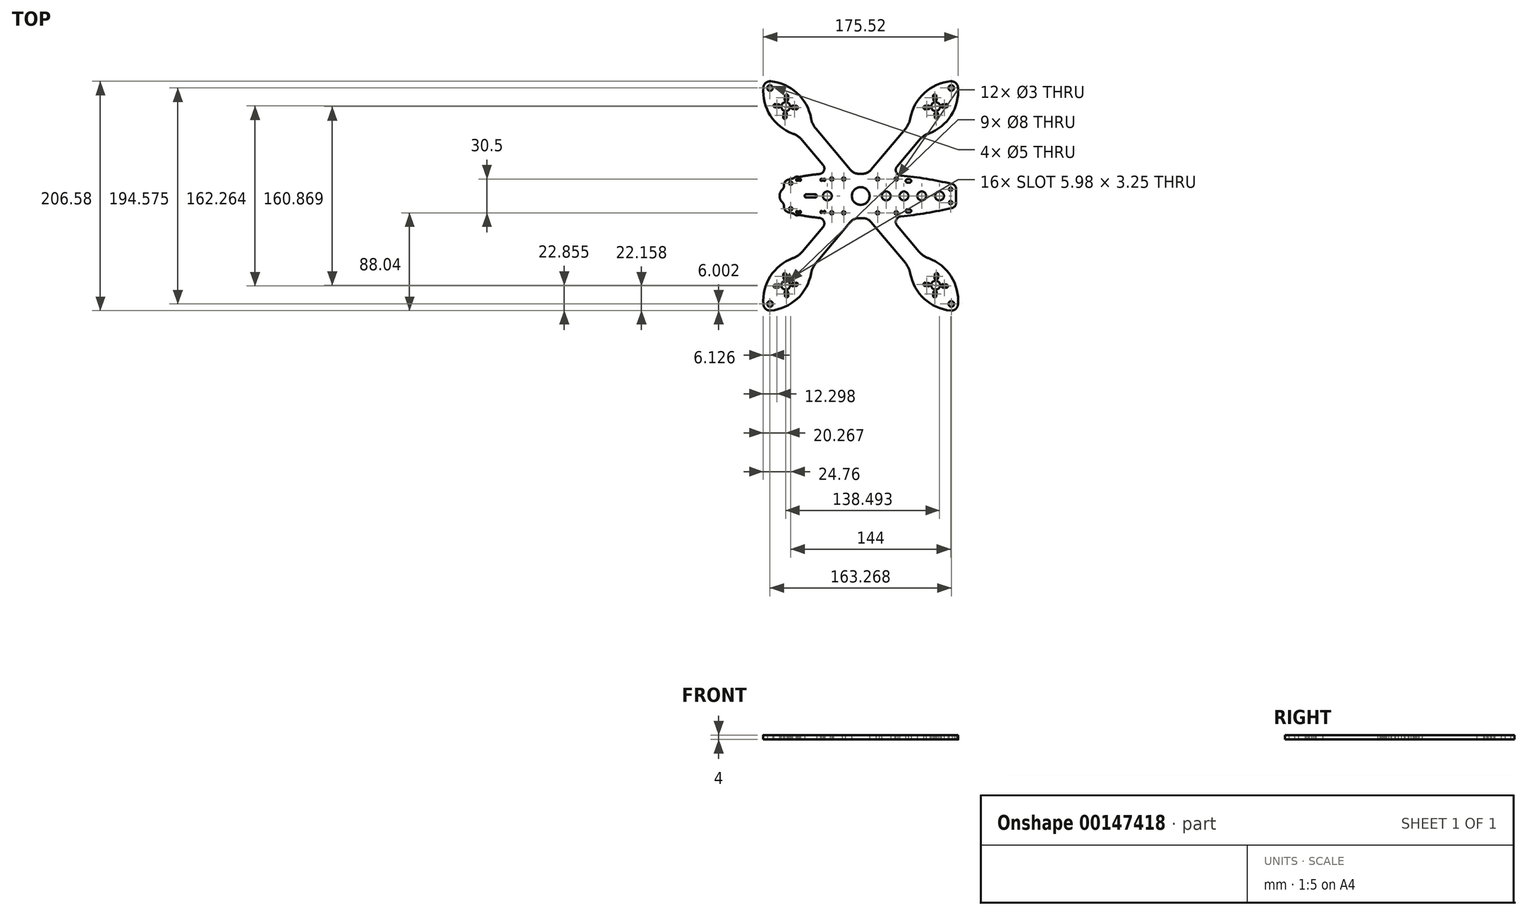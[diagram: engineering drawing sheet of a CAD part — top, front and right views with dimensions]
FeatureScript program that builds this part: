
annotation { "Feature Type Name" : "Feature", "Feature Type Description" : "" }
export const myFeature = defineFeature(function(context is Context, id is Id, definition is map)
    precondition{}
    {
        {
            var Q0;
            Q0=qCreatedBy(makeId("Top.planeOp"),FACE);
            var sketch = newSketch(context, id + "F0", { "sketchPlane" : qUnion([Q0])});
            skLineSegment(sketch, "E0.bottom", {"start": v(-1.68, 20) * mm, "end": v(1.68, 20) * mm});
            skLineSegment(sketch, "E0.left", {"start": v(-69, 9.77) * mm, "end": v(-69, 0) * mm});
            skLineSegment(sketch, "E0.right", {"start": v(86, 6.03) * mm, "end": v(86, 0) * mm});
            skArc(sketch, "E1", {"start": v(-15.25, 20) * mm, "mid": v(-16.05, 20.05) * mm, "end": v(-16.86, 20.09) * mm});
            skPoint(sketch, "E2.newPointA", {"position": v(-69, 13.5) * mm});
            skArc(sketch, "E2.filletArc", {"start": v(-65.37, 14.58) * mm, "mid": v(-67.99, 12.79) * mm, "end": v(-69, 9.77) * mm});
            skArc(sketch, "E3", {"start": v(82.11, 10.9) * mm, "mid": v(59.23, 15.39) * mm, "end": v(36.13, 18.46) * mm});
            skPoint(sketch, "E4.newPointA", {"position": v(86, 10) * mm});
            skArc(sketch, "E4.filletArc", {"start": v(86, 6.03) * mm, "mid": v(84.9, 9.15) * mm, "end": v(82.11, 10.9) * mm});
            skCircle(sketch, "E5", {"center": v(0, 0) * mm, "radius": 105 * mm, "construction": true});
            skLineSegment(sketch, "E6", {"start": v(0, 0) * mm, "end": v(67.5, 80.43) * mm, "construction": true});
            skLineSegment(sketch, "E7", {"start": v(0, 0) * mm, "end": v(-67.5, 80.43) * mm, "construction": true});
            skCircle(sketch, "E8", {"center": v(-67.5, 80.43) * mm, "radius": 4 * mm});
            skCircle(sketch, "E9", {"center": v(67.5, 80.43) * mm, "radius": 4 * mm});
            skCircle(sketch, "E10", {"center": v(-67.5, 80.43) * mm, "radius": 16 * mm, "construction": true});
            skCircle(sketch, "E11", {"center": v(67.5, 80.43) * mm, "radius": 16 * mm, "construction": true});
            skLineSegment(sketch, "E12", {"start": v(-40.3, 60.47) * mm, "end": v(-9.34, 23.57) * mm});
            skLineSegment(sketch, "E13.trimOffspring", {"start": v(-52.55, 50.19) * mm, "end": v(-33.87, 27.92) * mm});
            skArc(sketch, "E14.trimOffspring", {"start": v(-37.27, 19.73) * mm, "mid": v(-51.44, 17.82) * mm, "end": v(-65.37, 14.58) * mm});
            skPoint(sketch, "E15.visualSharp", {"position": v(-27.43, 20.25) * mm});
            skArc(sketch, "E15.filletArc", {"start": v(-37.27, 19.73) * mm, "mid": v(-33.09, 22.8) * mm, "end": v(-33.87, 27.92) * mm});
            skLineSegment(sketch, "E16", {"start": v(67.5, 80.43) * mm, "end": v(81.63, 97.29) * mm, "construction": true});
            skArc(sketch, "E17", {"start": v(87.61, 97.8) * mm, "mid": v(85.5, 101.88) * mm, "end": v(81.1, 103.26) * mm});
            skCircle(sketch, "E18", {"center": v(52.07, 62.05) * mm, "radius": 8 * mm, "construction": true});
            skArc(sketch, "E19", {"start": v(81.1, 103.26) * mm, "mid": v(57.22, 92.74) * mm, "end": v(44.67, 69.86) * mm});
            skArc(sketch, "E20", {"start": v(61.04, 56.13) * mm, "mid": v(81.4, 72.46) * mm, "end": v(87.61, 97.8) * mm});
            skLineSegment(sketch, "E21", {"start": v(40.3, 60.47) * mm, "end": v(9.34, 23.57) * mm});
            skLineSegment(sketch, "E22", {"start": v(52.55, 50.19) * mm, "end": v(32.8, 26.64) * mm});
            skPoint(sketch, "E23.newPointA", {"position": v(15.25, 20) * mm});
            skArc(sketch, "E23.filletArc", {"start": v(32.8, 26.64) * mm, "mid": v(32, 21.55) * mm, "end": v(36.13, 18.46) * mm});
            skArc(sketch, "E24.filletArc", {"start": v(1.68, 20) * mm, "mid": v(5.9, 20.94) * mm, "end": v(9.34, 23.57) * mm});
            skPoint(sketch, "E25.visualSharp", {"position": v(-6.34, 20) * mm});
            skArc(sketch, "E25.filletArc", {"start": v(-9.34, 23.57) * mm, "mid": v(-5.9, 20.94) * mm, "end": v(-1.68, 20) * mm});
            skArc(sketch, "E26.filletArc", {"start": v(61.04, 56.13) * mm, "mid": v(56.4, 53.71) * mm, "end": v(52.55, 50.19) * mm});
            skArc(sketch, "E27.filletArc", {"start": v(40.3, 60.47) * mm, "mid": v(43.1, 64.88) * mm, "end": v(44.67, 69.86) * mm});
            skCircle(sketch, "E28", {"center": v(81.63, 97.29) * mm, "radius": 2.5 * mm});
            skLineSegment(sketch, "E29", {"start": v(-67.5, 80.43) * mm, "end": v(-81.63, 97.29) * mm, "construction": true});
            skArc(sketch, "E30", {"start": v(-81.1, 103.26) * mm, "mid": v(-85.5, 101.88) * mm, "end": v(-87.61, 97.8) * mm});
            skCircle(sketch, "E31", {"center": v(-52.07, 62.05) * mm, "radius": 8 * mm, "construction": true});
            skArc(sketch, "E32", {"start": v(-87.61, 97.8) * mm, "mid": v(-81.4, 72.46) * mm, "end": v(-61.04, 56.13) * mm});
            skArc(sketch, "E33", {"start": v(-44.67, 69.86) * mm, "mid": v(-57.22, 92.74) * mm, "end": v(-81.1, 103.26) * mm});
            skArc(sketch, "E34.filletArc", {"start": v(-52.55, 50.19) * mm, "mid": v(-56.4, 53.71) * mm, "end": v(-61.04, 56.13) * mm});
            skArc(sketch, "E35.filletArc", {"start": v(-44.67, 69.86) * mm, "mid": v(-43.1, 64.88) * mm, "end": v(-40.3, 60.47) * mm});
            skCircle(sketch, "E36", {"center": v(-81.63, 97.29) * mm, "radius": 2.5 * mm});
            skLineSegment(sketch, "E37", {"start": v(-69, 0) * mm, "end": v(86, 0) * mm, "construction": true});
            skLineSegment(sketch, "E38.MirrorCS", {"start": v(0, 0) * mm, "end": v(-67.5, -80.43) * mm, "construction": true});
            skLineSegment(sketch, "E39.MirrorCS", {"start": v(0, 0) * mm, "end": v(67.5, -80.43) * mm, "construction": true});
            skLineSegment(sketch, "E40", {"start": v(-67.5, 80.43) * mm, "end": v(-66.1, 96.37) * mm, "construction": true});
            skArc(sketch, "E41", {"start": v(-68.42, 87.04) * mm, "mid": v(-67.06, 85.42) * mm, "end": v(-65.43, 86.78) * mm});
            skArc(sketch, "E42", {"start": v(-65.17, 89.77) * mm, "mid": v(-66.53, 91.4) * mm, "end": v(-68.16, 90.03) * mm});
            skLineSegment(sketch, "E43", {"start": v(-65.17, 89.77) * mm, "end": v(-65.43, 86.78) * mm});
            skLineSegment(sketch, "E44", {"start": v(-68.16, 90.03) * mm, "end": v(-68.42, 87.04) * mm});
            skArc(sketch, "E45.1.0", {"start": v(-74.1, 79.5) * mm, "mid": v(-72.47, 80.87) * mm, "end": v(-73.84, 82.5) * mm});
            skArc(sketch, "E45.1.1", {"start": v(-76.83, 82.76) * mm, "mid": v(-78.45, 81.4) * mm, "end": v(-77.09, 79.77) * mm});
            skLineSegment(sketch, "E45.1.2", {"start": v(-76.83, 82.76) * mm, "end": v(-73.84, 82.5) * mm});
            skLineSegment(sketch, "E45.1.3", {"start": v(-77.09, 79.77) * mm, "end": v(-74.1, 79.5) * mm});
            skArc(sketch, "E45.2.0", {"start": v(-66.56, 73.83) * mm, "mid": v(-67.93, 75.45) * mm, "end": v(-69.55, 74.1) * mm});
            skArc(sketch, "E45.2.1", {"start": v(-69.81, 71.1) * mm, "mid": v(-68.45, 69.48) * mm, "end": v(-66.83, 70.84) * mm});
            skLineSegment(sketch, "E45.2.2", {"start": v(-69.81, 71.1) * mm, "end": v(-69.55, 74.1) * mm});
            skLineSegment(sketch, "E45.2.3", {"start": v(-66.83, 70.84) * mm, "end": v(-66.56, 73.83) * mm});
            skArc(sketch, "E45.3.0", {"start": v(-60.89, 81.36) * mm, "mid": v(-62.51, 80) * mm, "end": v(-61.15, 78.37) * mm});
            skArc(sketch, "E45.3.1", {"start": v(-58.16, 78.11) * mm, "mid": v(-56.53, 79.48) * mm, "end": v(-57.9, 81.1) * mm});
            skLineSegment(sketch, "E45.3.2", {"start": v(-58.16, 78.11) * mm, "end": v(-61.15, 78.37) * mm});
            skLineSegment(sketch, "E45.3.3", {"start": v(-57.9, 81.1) * mm, "end": v(-60.89, 81.36) * mm});
            skLineSegment(sketch, "E46", {"start": v(67.5, 80.43) * mm, "end": v(83.43, 81.83) * mm, "construction": true});
            skArc(sketch, "E47", {"start": v(73.84, 82.5) * mm, "mid": v(72.47, 80.87) * mm, "end": v(74.1, 79.5) * mm});
            skArc(sketch, "E48", {"start": v(77.09, 79.77) * mm, "mid": v(78.45, 81.4) * mm, "end": v(76.83, 82.76) * mm});
            skLineSegment(sketch, "E49", {"start": v(73.84, 82.5) * mm, "end": v(76.83, 82.76) * mm});
            skLineSegment(sketch, "E50", {"start": v(77.09, 79.77) * mm, "end": v(74.1, 79.5) * mm});
            skLineSegment(sketch, "E51.1.0", {"start": v(65.43, 86.78) * mm, "end": v(65.17, 89.77) * mm});
            skArc(sketch, "E51.1.1", {"start": v(68.16, 90.03) * mm, "mid": v(66.53, 91.4) * mm, "end": v(65.17, 89.77) * mm});
            skArc(sketch, "E51.1.2", {"start": v(65.43, 86.78) * mm, "mid": v(67.06, 85.42) * mm, "end": v(68.42, 87.04) * mm});
            skLineSegment(sketch, "E51.1.3", {"start": v(68.16, 90.03) * mm, "end": v(68.42, 87.04) * mm});
            skLineSegment(sketch, "E51.2.0", {"start": v(61.15, 78.37) * mm, "end": v(58.16, 78.11) * mm});
            skArc(sketch, "E51.2.1", {"start": v(57.9, 81.1) * mm, "mid": v(56.53, 79.48) * mm, "end": v(58.16, 78.11) * mm});
            skArc(sketch, "E51.2.2", {"start": v(61.15, 78.37) * mm, "mid": v(62.51, 80) * mm, "end": v(60.89, 81.36) * mm});
            skLineSegment(sketch, "E51.2.3", {"start": v(57.9, 81.1) * mm, "end": v(60.89, 81.36) * mm});
            skLineSegment(sketch, "E51.3.0", {"start": v(69.55, 74.1) * mm, "end": v(69.81, 71.1) * mm});
            skArc(sketch, "E51.3.1", {"start": v(66.83, 70.84) * mm, "mid": v(68.45, 69.48) * mm, "end": v(69.81, 71.1) * mm});
            skArc(sketch, "E51.3.2", {"start": v(69.55, 74.1) * mm, "mid": v(67.93, 75.45) * mm, "end": v(66.56, 73.83) * mm});
            skLineSegment(sketch, "E51.3.3", {"start": v(66.83, 70.84) * mm, "end": v(66.56, 73.83) * mm});
            skLineSegment(sketch, "E52.MirrorCS", {"start": v(57.9, -81.1) * mm, "end": v(60.89, -81.36) * mm});
            skArc(sketch, "E53.MirrorCS", {"start": v(69.55, -74.1) * mm, "mid": v(67.93, -75.45) * mm, "end": v(66.56, -73.83) * mm});
            skLineSegment(sketch, "E54.MirrorCS", {"start": v(69.55, -74.1) * mm, "end": v(69.81, -71.1) * mm});
            skLineSegment(sketch, "E55.MirrorCS", {"start": v(73.84, -82.5) * mm, "end": v(76.83, -82.76) * mm});
            skLineSegment(sketch, "E56.MirrorCS", {"start": v(-65.17, -89.77) * mm, "end": v(-65.43, -86.78) * mm});
            skArc(sketch, "E57.MirrorCS", {"start": v(77.09, -79.77) * mm, "mid": v(78.45, -81.4) * mm, "end": v(76.83, -82.76) * mm});
            skLineSegment(sketch, "E58.MirrorCS", {"start": v(-68.16, -90.03) * mm, "end": v(-68.42, -87.04) * mm});
            skArc(sketch, "E59.MirrorCS", {"start": v(73.84, -82.5) * mm, "mid": v(72.47, -80.87) * mm, "end": v(74.1, -79.5) * mm});
            skLineSegment(sketch, "E60.MirrorCS", {"start": v(66.83, -70.84) * mm, "end": v(66.56, -73.83) * mm});
            skArc(sketch, "E61.MirrorCS", {"start": v(-65.17, -89.77) * mm, "mid": v(-66.53, -91.4) * mm, "end": v(-68.16, -90.03) * mm});
            skLineSegment(sketch, "E62.MirrorCS", {"start": v(77.09, -79.77) * mm, "end": v(74.1, -79.5) * mm});
            skArc(sketch, "E63.MirrorCS", {"start": v(-68.42, -87.04) * mm, "mid": v(-67.06, -85.42) * mm, "end": v(-65.43, -86.78) * mm});
            skLineSegment(sketch, "E64.MirrorCS", {"start": v(-57.9, -81.1) * mm, "end": v(-60.89, -81.36) * mm});
            skLineSegment(sketch, "E65.MirrorCS", {"start": v(-1.68, -20) * mm, "end": v(1.68, -20) * mm});
            skArc(sketch, "E66.MirrorCS", {"start": v(1.68, -20) * mm, "mid": v(5.9, -20.94) * mm, "end": v(9.34, -23.57) * mm});
            skLineSegment(sketch, "E67.MirrorCS", {"start": v(-58.16, -78.11) * mm, "end": v(-61.15, -78.37) * mm});
            skArc(sketch, "E68.MirrorCS", {"start": v(65.43, -86.78) * mm, "mid": v(67.06, -85.42) * mm, "end": v(68.42, -87.04) * mm});
            skLineSegment(sketch, "E69.MirrorCS", {"start": v(-77.09, -79.77) * mm, "end": v(-74.1, -79.5) * mm});
            skArc(sketch, "E70.MirrorCS", {"start": v(-76.83, -82.76) * mm, "mid": v(-78.45, -81.4) * mm, "end": v(-77.09, -79.77) * mm});
            skLineSegment(sketch, "E71.MirrorCS", {"start": v(86, -6.03) * mm, "end": v(86, 0) * mm});
            skArc(sketch, "E72.MirrorCS", {"start": v(68.16, -90.03) * mm, "mid": v(66.53, -91.4) * mm, "end": v(65.17, -89.77) * mm});
            skArc(sketch, "E73.MirrorCS", {"start": v(-74.1, -79.5) * mm, "mid": v(-72.47, -80.87) * mm, "end": v(-73.84, -82.5) * mm});
            skArc(sketch, "E74.MirrorCS", {"start": v(86, -6.03) * mm, "mid": v(84.9, -9.15) * mm, "end": v(82.11, -10.9) * mm});
            skArc(sketch, "E75.MirrorCS", {"start": v(-66.56, -73.83) * mm, "mid": v(-67.93, -75.45) * mm, "end": v(-69.55, -74.1) * mm});
            skLineSegment(sketch, "E76.MirrorCS", {"start": v(-66.83, -70.84) * mm, "end": v(-66.56, -73.83) * mm});
            skArc(sketch, "E77.MirrorCS", {"start": v(-69.81, -71.1) * mm, "mid": v(-68.45, -69.48) * mm, "end": v(-66.83, -70.84) * mm});
            skArc(sketch, "E78.MirrorCS", {"start": v(57.9, -81.1) * mm, "mid": v(56.53, -79.48) * mm, "end": v(58.16, -78.11) * mm});
            skLineSegment(sketch, "E79.MirrorCS", {"start": v(-76.83, -82.76) * mm, "end": v(-73.84, -82.5) * mm});
            skArc(sketch, "E80.MirrorCS", {"start": v(61.15, -78.37) * mm, "mid": v(62.51, -80) * mm, "end": v(60.89, -81.36) * mm});
            skCircle(sketch, "E81.MirrorC", {"center": v(-67.5, -80.43) * mm, "radius": 4 * mm});
            skCircle(sketch, "E82.MirrorC", {"center": v(67.5, -80.43) * mm, "radius": 4 * mm});
            skArc(sketch, "E83.MirrorCS", {"start": v(66.83, -70.84) * mm, "mid": v(68.45, -69.48) * mm, "end": v(69.81, -71.1) * mm});
            skLineSegment(sketch, "E84.MirrorCS", {"start": v(-69.81, -71.1) * mm, "end": v(-69.55, -74.1) * mm});
            skArc(sketch, "E85.MirrorCS", {"start": v(-65.37, -14.58) * mm, "mid": v(-67.99, -12.79) * mm, "end": v(-69, -9.77) * mm});
            skLineSegment(sketch, "E86.MirrorCS", {"start": v(68.16, -90.03) * mm, "end": v(68.42, -87.04) * mm});
            skArc(sketch, "E87.MirrorCS", {"start": v(-60.89, -81.36) * mm, "mid": v(-62.51, -80) * mm, "end": v(-61.15, -78.37) * mm});
            skLineSegment(sketch, "E88.MirrorCS", {"start": v(65.43, -86.78) * mm, "end": v(65.17, -89.77) * mm});
            skLineSegment(sketch, "E89.MirrorCS", {"start": v(61.15, -78.37) * mm, "end": v(58.16, -78.11) * mm});
            skArc(sketch, "E90.MirrorCS", {"start": v(-58.16, -78.11) * mm, "mid": v(-56.53, -79.48) * mm, "end": v(-57.9, -81.1) * mm});
            skLineSegment(sketch, "E91.MirrorCS", {"start": v(-67.5, -80.43) * mm, "end": v(-66.1, -96.37) * mm, "construction": true});
            skLineSegment(sketch, "E92.MirrorCS", {"start": v(-69, -9.77) * mm, "end": v(-69, 0) * mm});
            skArc(sketch, "E93.MirrorCS", {"start": v(-9.34, -23.57) * mm, "mid": v(-5.9, -20.94) * mm, "end": v(-1.68, -20) * mm});
            skArc(sketch, "E94.MirrorCS", {"start": v(-15.25, -20) * mm, "mid": v(-16.05, -20.05) * mm, "end": v(-16.86, -20.09) * mm});
            skLineSegment(sketch, "E95.MirrorCS", {"start": v(67.5, -80.43) * mm, "end": v(83.43, -81.83) * mm, "construction": true});
            skArc(sketch, "E96.MirrorCS", {"start": v(61.04, -56.13) * mm, "mid": v(81.4, -72.46) * mm, "end": v(87.61, -97.8) * mm});
            skLineSegment(sketch, "E97.MirrorCS", {"start": v(-40.3, -60.47) * mm, "end": v(-9.34, -23.57) * mm});
            skPoint(sketch, "E98.MirrorP", {"position": v(86, -10) * mm});
            skArc(sketch, "E99.MirrorCS", {"start": v(32.8, -26.64) * mm, "mid": v(32, -21.55) * mm, "end": v(36.13, -18.46) * mm});
            skArc(sketch, "E100.MirrorCS", {"start": v(-44.67, -69.86) * mm, "mid": v(-57.22, -92.74) * mm, "end": v(-81.1, -103.26) * mm});
            skPoint(sketch, "E101.MirrorP", {"position": v(-27.43, -20.25) * mm});
            skPoint(sketch, "E102.MirrorP", {"position": v(-69, -13.5) * mm});
            skCircle(sketch, "E103.MirrorC", {"center": v(81.63, -97.29) * mm, "radius": 2.5 * mm});
            skPoint(sketch, "E104.MirrorP", {"position": v(15.25, -20) * mm});
            skLineSegment(sketch, "E105.MirrorCS", {"start": v(67.5, -80.43) * mm, "end": v(81.63, -97.29) * mm, "construction": true});
            skArc(sketch, "E106.MirrorCS", {"start": v(81.1, -103.26) * mm, "mid": v(57.22, -92.74) * mm, "end": v(44.67, -69.86) * mm});
            skArc(sketch, "E107.MirrorCS", {"start": v(-37.27, -19.73) * mm, "mid": v(-33.09, -22.8) * mm, "end": v(-33.87, -27.92) * mm});
            skPoint(sketch, "E108.MirrorP", {"position": v(-6.34, -20) * mm});
            skArc(sketch, "E109.MirrorCS", {"start": v(87.61, -97.8) * mm, "mid": v(85.5, -101.88) * mm, "end": v(81.1, -103.26) * mm});
            skCircle(sketch, "E110.MirrorC", {"center": v(-81.63, -97.29) * mm, "radius": 2.5 * mm});
            skArc(sketch, "E111.MirrorCS", {"start": v(-37.27, -19.73) * mm, "mid": v(-51.44, -17.82) * mm, "end": v(-65.37, -14.58) * mm});
            skCircle(sketch, "E112.MirrorC", {"center": v(52.07, -62.05) * mm, "radius": 8 * mm, "construction": true});
            skCircle(sketch, "E113.MirrorC", {"center": v(67.5, -80.43) * mm, "radius": 16 * mm, "construction": true});
            skLineSegment(sketch, "E114.MirrorCS", {"start": v(52.55, -50.19) * mm, "end": v(32.8, -26.64) * mm});
            skCircle(sketch, "E115.MirrorC", {"center": v(-67.5, -80.43) * mm, "radius": 16 * mm, "construction": true});
            skArc(sketch, "E116.MirrorCS", {"start": v(-52.55, -50.19) * mm, "mid": v(-56.4, -53.71) * mm, "end": v(-61.04, -56.13) * mm});
            skLineSegment(sketch, "E117.MirrorCS", {"start": v(-52.55, -50.19) * mm, "end": v(-33.87, -27.92) * mm});
            skArc(sketch, "E118.MirrorCS", {"start": v(-87.61, -97.8) * mm, "mid": v(-81.4, -72.46) * mm, "end": v(-61.04, -56.13) * mm});
            skArc(sketch, "E119.MirrorCS", {"start": v(-44.67, -69.86) * mm, "mid": v(-43.1, -64.88) * mm, "end": v(-40.3, -60.47) * mm});
            skCircle(sketch, "E120.MirrorC", {"center": v(-52.07, -62.05) * mm, "radius": 8 * mm, "construction": true});
            skArc(sketch, "E121.MirrorCS", {"start": v(40.3, -60.47) * mm, "mid": v(43.1, -64.88) * mm, "end": v(44.67, -69.86) * mm});
            skLineSegment(sketch, "E122.MirrorCS", {"start": v(-67.5, -80.43) * mm, "end": v(-81.63, -97.29) * mm, "construction": true});
            skArc(sketch, "E123.MirrorCS", {"start": v(61.04, -56.13) * mm, "mid": v(56.4, -53.71) * mm, "end": v(52.55, -50.19) * mm});
            skArc(sketch, "E124.MirrorCS", {"start": v(82.11, -10.9) * mm, "mid": v(59.23, -15.39) * mm, "end": v(36.13, -18.46) * mm});
            skArc(sketch, "E125.MirrorCS", {"start": v(-81.1, -103.26) * mm, "mid": v(-85.5, -101.88) * mm, "end": v(-87.61, -97.8) * mm});
            skLineSegment(sketch, "E126.MirrorCS", {"start": v(40.3, -60.47) * mm, "end": v(9.34, -23.57) * mm});
            skCircle(sketch, "E127", {"center": v(-15.25, 15.25) * mm, "radius": 1.5 * mm});
            skCircle(sketch, "E128.0.1.0", {"center": v(-15.25, -15.25) * mm, "radius": 1.5 * mm});
            skCircle(sketch, "E128.1.0.0", {"center": v(15.25, 15.25) * mm, "radius": 1.5 * mm});
            skCircle(sketch, "E128.1.1.0", {"center": v(15.25, -15.25) * mm, "radius": 1.5 * mm});
            skLineSegment(sketch, "E128.direction1", {"start": v(-15.25, 15.25) * mm, "end": v(15.25, 15.25) * mm, "construction": true});
            skLineSegment(sketch, "E128.direction2", {"start": v(-15.25, 15.25) * mm, "end": v(-15.25, -15.25) * mm, "construction": true});
            skCircle(sketch, "E129", {"center": v(-26, 15.25) * mm, "radius": 1.5 * mm});
            skCircle(sketch, "E130.0.1.0", {"center": v(-26, -15.25) * mm, "radius": 1.5 * mm});
            skCircle(sketch, "E130.1.0.0", {"center": v(32, 15.25) * mm, "radius": 1.5 * mm});
            skCircle(sketch, "E130.1.1.0", {"center": v(32, -15.25) * mm, "radius": 1.5 * mm});
            skLineSegment(sketch, "E130.direction1", {"start": v(-26, 15.25) * mm, "end": v(32, 15.25) * mm, "construction": true});
            skLineSegment(sketch, "E130.direction2", {"start": v(-26, 15.25) * mm, "end": v(-26, -15.25) * mm, "construction": true});
            skCircle(sketch, "E131", {"center": v(-63, 11.5) * mm, "radius": 1.5 * mm});
            skCircle(sketch, "E132.MirrorC", {"center": v(-63, -11.5) * mm, "radius": 1.5 * mm});
            skCircle(sketch, "E133", {"center": v(67.5, -80.43) * mm, "radius": 63.5 * mm, "construction": true});
            skCircle(sketch, "E134", {"center": v(67.5, 80.43) * mm, "radius": 63.5 * mm, "construction": true});
            skCircle(sketch, "E135", {"center": v(-67.5, -80.43) * mm, "radius": 63.5 * mm, "construction": true});
            skCircle(sketch, "E136", {"center": v(-67.5, 80.43) * mm, "radius": 63.5 * mm, "construction": true});
            skCircle(sketch, "E137", {"center": v(81, 6) * mm, "radius": 1.5 * mm});
            skCircle(sketch, "E138", {"center": v(81, -6) * mm, "radius": 1.5 * mm});
            skLineSegment(sketch, "E139", {"start": v(81, 6.03) * mm, "end": v(81, 6) * mm, "construction": true});
            skLineSegment(sketch, "E140", {"start": v(81, -6.03) * mm, "end": v(81, -6) * mm, "construction": true});
            skSolve(sketch);
        }
        {
            var Q0;
            Q0=qSketchRegion(id+"F0",true);
            extrude(context, id + "F1", {"entities" : qUnion([Q0]), "depth" : 4 * mm});
        }
        {
            var Q0;
            Q0=qCreatedBy(makeId("Top.planeOp"),FACE);
            var sketch = newSketch(context, id + "F2", { "sketchPlane" : qUnion([Q0])});
            skLineSegment(sketch, "E141.bottom", {"start": v(-49, 1.5) * mm, "end": v(-41, 1.5) * mm});
            skLineSegment(sketch, "E141.top", {"start": v(-49, -1.5) * mm, "end": v(-41, -1.5) * mm});
            skArc(sketch, "E142", {"start": v(-49, 1.5) * mm, "mid": v(-50.5, 0) * mm, "end": v(-49, -1.5) * mm});
            skArc(sketch, "E143", {"start": v(-41, -1.5) * mm, "mid": v(-39.5, 0) * mm, "end": v(-41, 1.5) * mm});
            skLineSegment(sketch, "E144", {"start": v(-49, 1.5) * mm, "end": v(-49, 0) * mm, "construction": true});
            skLineSegment(sketch, "E145.bottom", {"start": v(42, 15) * mm, "end": v(44, 15) * mm});
            skLineSegment(sketch, "E145.top", {"start": v(42, 12) * mm, "end": v(44, 12) * mm});
            skLineSegment(sketch, "E145.left", {"start": v(42, 15) * mm, "end": v(42, 12) * mm});
            skLineSegment(sketch, "E145.right", {"start": v(44, 15) * mm, "end": v(44, 12) * mm});
            skLineSegment(sketch, "E146.bottom", {"start": v(42, -12) * mm, "end": v(44, -12) * mm});
            skLineSegment(sketch, "E146.top", {"start": v(42, -15) * mm, "end": v(44, -15) * mm});
            skLineSegment(sketch, "E146.left", {"start": v(42, -12) * mm, "end": v(42, -15) * mm});
            skLineSegment(sketch, "E146.right", {"start": v(44, -12) * mm, "end": v(44, -15) * mm});
            skArc(sketch, "E147", {"start": v(44, 12) * mm, "mid": v(45.5, 13.5) * mm, "end": v(44, 15) * mm});
            skArc(sketch, "E148", {"start": v(42, 15) * mm, "mid": v(40.5, 13.5) * mm, "end": v(42, 12) * mm});
            skArc(sketch, "E149", {"start": v(42, -12) * mm, "mid": v(40.5, -13.5) * mm, "end": v(42, -15) * mm});
            skArc(sketch, "E150", {"start": v(44, -15) * mm, "mid": v(45.5, -13.5) * mm, "end": v(44, -12) * mm});
            skLineSegment(sketch, "E151.direction1", {"start": v(42, -15) * mm, "end": v(58, -15) * mm, "construction": true});
            skCircle(sketch, "E152", {"center": v(55, 0) * mm, "radius": 4 * mm});
            skCircle(sketch, "E153", {"center": v(71, 0) * mm, "radius": 4 * mm});
            skCircle(sketch, "E154", {"center": v(39, 0) * mm, "radius": 4 * mm});
            skCircle(sketch, "E155", {"center": v(0, 0) * mm, "radius": 8 * mm});
            skCircle(sketch, "E156", {"center": v(-30, 0) * mm, "radius": 4 * mm});
            skCircle(sketch, "E157", {"center": v(23, 0) * mm, "radius": 4 * mm});
            skSolve(sketch);
        }
        {
            var Q0;
            Q0=qSketchRegion(id+"F2",true);
            extrude(context, id + "F3", {"entities" : qUnion([Q0]), "operationType" : NewBodyOperationType.REMOVE, "depth" : 25 * mm});
        }
        {
            var Q0;
            Q0=makeQuery(id+"F1.opExtrude","CAP_FACE",FACE,{"disambiguationData":[OSD([sQuery(id+"F0.wireOp",EDGE,"E0.bottom"),sQuery(id+"F0.wireOp",EDGE,"E0.left"),sQuery(id+"F0.wireOp",EDGE,"E0.right"),sQuery(id+"F0.wireOp",EDGE,"E2.filletArc"),sQuery(id+"F0.wireOp",EDGE,"E3"),sQuery(id+"F0.wireOp",EDGE,"E4.filletArc"),sQuery(id+"F0.wireOp",EDGE,"E8"),sQuery(id+"F0.wireOp",EDGE,"E9"),sQuery(id+"F0.wireOp",EDGE,"E12"),sQuery(id+"F0.wireOp",EDGE,"E13.trimOffspring"),sQuery(id+"F0.wireOp",EDGE,"E14.trimOffspring"),sQuery(id+"F0.wireOp",EDGE,"E15.filletArc"),sQuery(id+"F0.wireOp",EDGE,"E17"),sQuery(id+"F0.wireOp",EDGE,"E19"),sQuery(id+"F0.wireOp",EDGE,"E20"),sQuery(id+"F0.wireOp",EDGE,"E21"),sQuery(id+"F0.wireOp",EDGE,"E22"),sQuery(id+"F0.wireOp",EDGE,"E23.filletArc"),sQuery(id+"F0.wireOp",EDGE,"E24.filletArc"),sQuery(id+"F0.wireOp",EDGE,"E25.filletArc"),sQuery(id+"F0.wireOp",EDGE,"E26.filletArc"),sQuery(id+"F0.wireOp",EDGE,"E27.filletArc"),sQuery(id+"F0.wireOp",EDGE,"E28"),sQuery(id+"F0.wireOp",EDGE,"E30"),sQuery(id+"F0.wireOp",EDGE,"E32"),sQuery(id+"F0.wireOp",EDGE,"E33"),sQuery(id+"F0.wireOp",EDGE,"E34.filletArc"),sQuery(id+"F0.wireOp",EDGE,"E35.filletArc"),sQuery(id+"F0.wireOp",EDGE,"E36"),sQuery(id+"F0.wireOp",EDGE,"E41"),sQuery(id+"F0.wireOp",EDGE,"E42"),sQuery(id+"F0.wireOp",EDGE,"E43"),sQuery(id+"F0.wireOp",EDGE,"E44"),sQuery(id+"F0.wireOp",EDGE,"E45.1.0"),sQuery(id+"F0.wireOp",EDGE,"E45.1.1"),sQuery(id+"F0.wireOp",EDGE,"E45.1.2"),sQuery(id+"F0.wireOp",EDGE,"E45.1.3"),sQuery(id+"F0.wireOp",EDGE,"E45.2.0"),sQuery(id+"F0.wireOp",EDGE,"E45.2.1"),sQuery(id+"F0.wireOp",EDGE,"E45.2.2"),sQuery(id+"F0.wireOp",EDGE,"E45.2.3"),sQuery(id+"F0.wireOp",EDGE,"E45.3.0"),sQuery(id+"F0.wireOp",EDGE,"E45.3.1"),sQuery(id+"F0.wireOp",EDGE,"E45.3.2"),sQuery(id+"F0.wireOp",EDGE,"E45.3.3"),sQuery(id+"F0.wireOp",EDGE,"E47"),sQuery(id+"F0.wireOp",EDGE,"E48"),sQuery(id+"F0.wireOp",EDGE,"E49"),sQuery(id+"F0.wireOp",EDGE,"E50"),sQuery(id+"F0.wireOp",EDGE,"E51.1.0"),sQuery(id+"F0.wireOp",EDGE,"E51.1.1"),sQuery(id+"F0.wireOp",EDGE,"E51.1.2"),sQuery(id+"F0.wireOp",EDGE,"E51.1.3"),sQuery(id+"F0.wireOp",EDGE,"E51.2.0"),sQuery(id+"F0.wireOp",EDGE,"E51.2.1"),sQuery(id+"F0.wireOp",EDGE,"E51.2.2"),sQuery(id+"F0.wireOp",EDGE,"E51.2.3"),sQuery(id+"F0.wireOp",EDGE,"E51.3.0"),sQuery(id+"F0.wireOp",EDGE,"E51.3.1"),sQuery(id+"F0.wireOp",EDGE,"E51.3.2"),sQuery(id+"F0.wireOp",EDGE,"E51.3.3"),sQuery(id+"F0.wireOp",EDGE,"E52.MirrorCS"),sQuery(id+"F0.wireOp",EDGE,"E53.MirrorCS"),sQuery(id+"F0.wireOp",EDGE,"E54.MirrorCS"),sQuery(id+"F0.wireOp",EDGE,"E55.MirrorCS"),sQuery(id+"F0.wireOp",EDGE,"E56.MirrorCS"),sQuery(id+"F0.wireOp",EDGE,"E57.MirrorCS"),sQuery(id+"F0.wireOp",EDGE,"E58.MirrorCS"),sQuery(id+"F0.wireOp",EDGE,"E59.MirrorCS"),sQuery(id+"F0.wireOp",EDGE,"E60.MirrorCS"),sQuery(id+"F0.wireOp",EDGE,"E61.MirrorCS"),sQuery(id+"F0.wireOp",EDGE,"E62.MirrorCS"),sQuery(id+"F0.wireOp",EDGE,"E63.MirrorCS"),sQuery(id+"F0.wireOp",EDGE,"E64.MirrorCS"),sQuery(id+"F0.wireOp",EDGE,"E65.MirrorCS"),sQuery(id+"F0.wireOp",EDGE,"E66.MirrorCS"),sQuery(id+"F0.wireOp",EDGE,"E67.MirrorCS"),sQuery(id+"F0.wireOp",EDGE,"E68.MirrorCS"),sQuery(id+"F0.wireOp",EDGE,"E69.MirrorCS"),sQuery(id+"F0.wireOp",EDGE,"E70.MirrorCS"),sQuery(id+"F0.wireOp",EDGE,"E71.MirrorCS"),sQuery(id+"F0.wireOp",EDGE,"E72.MirrorCS"),sQuery(id+"F0.wireOp",EDGE,"E73.MirrorCS"),sQuery(id+"F0.wireOp",EDGE,"E74.MirrorCS"),sQuery(id+"F0.wireOp",EDGE,"E75.MirrorCS"),sQuery(id+"F0.wireOp",EDGE,"E76.MirrorCS"),sQuery(id+"F0.wireOp",EDGE,"E77.MirrorCS"),sQuery(id+"F0.wireOp",EDGE,"E78.MirrorCS"),sQuery(id+"F0.wireOp",EDGE,"E79.MirrorCS"),sQuery(id+"F0.wireOp",EDGE,"E80.MirrorCS"),sQuery(id+"F0.wireOp",EDGE,"E81.MirrorC"),sQuery(id+"F0.wireOp",EDGE,"E82.MirrorC"),sQuery(id+"F0.wireOp",EDGE,"E83.MirrorCS"),sQuery(id+"F0.wireOp",EDGE,"E84.MirrorCS"),sQuery(id+"F0.wireOp",EDGE,"E85.MirrorCS"),sQuery(id+"F0.wireOp",EDGE,"E86.MirrorCS"),sQuery(id+"F0.wireOp",EDGE,"E87.MirrorCS"),sQuery(id+"F0.wireOp",EDGE,"E88.MirrorCS"),sQuery(id+"F0.wireOp",EDGE,"E89.MirrorCS"),sQuery(id+"F0.wireOp",EDGE,"E90.MirrorCS"),sQuery(id+"F0.wireOp",EDGE,"E92.MirrorCS"),sQuery(id+"F0.wireOp",EDGE,"E93.MirrorCS"),sQuery(id+"F0.wireOp",EDGE,"E96.MirrorCS"),sQuery(id+"F0.wireOp",EDGE,"E97.MirrorCS"),sQuery(id+"F0.wireOp",EDGE,"E99.MirrorCS"),sQuery(id+"F0.wireOp",EDGE,"E100.MirrorCS"),sQuery(id+"F0.wireOp",EDGE,"E103.MirrorC"),sQuery(id+"F0.wireOp",EDGE,"E106.MirrorCS"),sQuery(id+"F0.wireOp",EDGE,"E107.MirrorCS"),sQuery(id+"F0.wireOp",EDGE,"E109.MirrorCS"),sQuery(id+"F0.wireOp",EDGE,"E110.MirrorC"),sQuery(id+"F0.wireOp",EDGE,"E111.MirrorCS"),sQuery(id+"F0.wireOp",EDGE,"E114.MirrorCS"),sQuery(id+"F0.wireOp",EDGE,"E116.MirrorCS"),sQuery(id+"F0.wireOp",EDGE,"E117.MirrorCS"),sQuery(id+"F0.wireOp",EDGE,"E118.MirrorCS"),sQuery(id+"F0.wireOp",EDGE,"E119.MirrorCS"),sQuery(id+"F0.wireOp",EDGE,"E121.MirrorCS"),sQuery(id+"F0.wireOp",EDGE,"E123.MirrorCS"),sQuery(id+"F0.wireOp",EDGE,"E124.MirrorCS"),sQuery(id+"F0.wireOp",EDGE,"E125.MirrorCS"),sQuery(id+"F0.wireOp",EDGE,"E126.MirrorCS"),sQuery(id+"F0.wireOp",EDGE,"E127"),sQuery(id+"F0.wireOp",EDGE,"E128.0.1.0"),sQuery(id+"F0.wireOp",EDGE,"E128.1.0.0"),sQuery(id+"F0.wireOp",EDGE,"E128.1.1.0"),sQuery(id+"F0.wireOp",EDGE,"E129"),sQuery(id+"F0.wireOp",EDGE,"E130.0.1.0"),sQuery(id+"F0.wireOp",EDGE,"E130.1.0.0"),sQuery(id+"F0.wireOp",EDGE,"E130.1.1.0"),sQuery(id+"F0.wireOp",EDGE,"2X2VCuhx-sfNE-qQAx-ANOA-V8PgWdT9DL1t"),sQuery(id+"F0.wireOp",EDGE,"EbufiATG-6Epo-heG6-67Bm-3WETjLEGOB6e"),sQuery(id+"F0.wireOp",EDGE,"E131"),sQuery(id+"F0.wireOp",EDGE,"E132.MirrorC")])],"isStart":false});
            var sketch = newSketch(context, id + "F4", { "sketchPlane" : qUnion([Q0])});
            skLineSegment(sketch, "E158.top", {"start": v(-57, 14) * mm, "end": v(-55, 14) * mm});
            skLineSegment(sketch, "E159.right", {"start": v(-54, 15) * mm, "end": v(-54, 14) * mm});
            skLineSegment(sketch, "E160.left", {"start": v(-58, 15) * mm, "end": v(-58, 14) * mm});
            skArc(sketch, "E161", {"start": v(-57, 15) * mm, "mid": v(-57.5, 15.5) * mm, "end": v(-58, 15) * mm});
            skArc(sketch, "E162", {"start": v(-54, 15) * mm, "mid": v(-54.5, 15.5) * mm, "end": v(-55, 15) * mm});
            skArc(sketch, "E163", {"start": v(-55, 14) * mm, "mid": v(-54.5, 13.5) * mm, "end": v(-54, 14) * mm});
            skArc(sketch, "E164", {"start": v(-58, 14) * mm, "mid": v(-57.5, 13.5) * mm, "end": v(-57, 14) * mm});
            skLineSegment(sketch, "E165", {"start": v(-57, 15) * mm, "end": v(-55, 15) * mm});
            skLineSegment(sketch, "E166.0.1.0", {"start": v(-57, -15) * mm, "end": v(-55, -15) * mm});
            skLineSegment(sketch, "E166.0.1.1", {"start": v(-57, -14) * mm, "end": v(-55, -14) * mm});
            skLineSegment(sketch, "E166.0.1.2", {"start": v(-54, -14) * mm, "end": v(-54, -15) * mm});
            skLineSegment(sketch, "E166.0.1.3", {"start": v(-58, -14) * mm, "end": v(-58, -15) * mm});
            skArc(sketch, "E166.0.1.4", {"start": v(-57, -14) * mm, "mid": v(-57.5, -13.5) * mm, "end": v(-58, -14) * mm});
            skArc(sketch, "E166.0.1.5", {"start": v(-58, -15) * mm, "mid": v(-57.5, -15.5) * mm, "end": v(-57, -15) * mm});
            skArc(sketch, "E166.0.1.6", {"start": v(-55, -15) * mm, "mid": v(-54.5, -15.5) * mm, "end": v(-54, -15) * mm});
            skArc(sketch, "E166.0.1.7", {"start": v(-54, -14) * mm, "mid": v(-54.5, -13.5) * mm, "end": v(-55, -14) * mm});
            skLineSegment(sketch, "E166.1.0.0", {"start": v(-35, 14) * mm, "end": v(-33, 14) * mm});
            skLineSegment(sketch, "E166.1.0.1", {"start": v(-35, 15) * mm, "end": v(-33, 15) * mm});
            skLineSegment(sketch, "E166.1.0.2", {"start": v(-32, 15) * mm, "end": v(-32, 14) * mm});
            skLineSegment(sketch, "E166.1.0.3", {"start": v(-36, 15) * mm, "end": v(-36, 14) * mm});
            skArc(sketch, "E166.1.0.4", {"start": v(-35, 15) * mm, "mid": v(-35.5, 15.5) * mm, "end": v(-36, 15) * mm});
            skArc(sketch, "E166.1.0.5", {"start": v(-36, 14) * mm, "mid": v(-35.5, 13.5) * mm, "end": v(-35, 14) * mm});
            skArc(sketch, "E166.1.0.6", {"start": v(-33, 14) * mm, "mid": v(-32.5, 13.5) * mm, "end": v(-32, 14) * mm});
            skArc(sketch, "E166.1.0.7", {"start": v(-32, 15) * mm, "mid": v(-32.5, 15.5) * mm, "end": v(-33, 15) * mm});
            skLineSegment(sketch, "E166.1.1.0", {"start": v(-35, -15) * mm, "end": v(-33, -15) * mm});
            skLineSegment(sketch, "E166.1.1.1", {"start": v(-35, -14) * mm, "end": v(-33, -14) * mm});
            skLineSegment(sketch, "E166.1.1.2", {"start": v(-32, -14) * mm, "end": v(-32, -15) * mm});
            skLineSegment(sketch, "E166.1.1.3", {"start": v(-36, -14) * mm, "end": v(-36, -15) * mm});
            skArc(sketch, "E166.1.1.4", {"start": v(-35, -14) * mm, "mid": v(-35.5, -13.5) * mm, "end": v(-36, -14) * mm});
            skArc(sketch, "E166.1.1.5", {"start": v(-36, -15) * mm, "mid": v(-35.5, -15.5) * mm, "end": v(-35, -15) * mm});
            skArc(sketch, "E166.1.1.6", {"start": v(-33, -15) * mm, "mid": v(-32.5, -15.5) * mm, "end": v(-32, -15) * mm});
            skArc(sketch, "E166.1.1.7", {"start": v(-32, -14) * mm, "mid": v(-32.5, -13.5) * mm, "end": v(-33, -14) * mm});
            skLineSegment(sketch, "E166.direction1", {"start": v(-58, 14) * mm, "end": v(-36, 14) * mm, "construction": true});
            skLineSegment(sketch, "E166.direction2", {"start": v(-58, 14) * mm, "end": v(-58, -15) * mm, "construction": true});
            skSolve(sketch);
        }
        {
            var Q0;
            Q0=qSketchRegion(id+"F4",true);
            extrude(context, id + "F5", {"entities" : qUnion([Q0]), "operationType" : NewBodyOperationType.REMOVE, "oppositeDirection" : true, "depth" : 25 * mm});
        }
        {
            var Q0;
            Q0=makeQuery(id+"F1.opExtrude","CAP_FACE",FACE,{"disambiguationData":[OSD([sQuery(id+"F0.wireOp",EDGE,"E0.bottom"),sQuery(id+"F0.wireOp",EDGE,"E0.left"),sQuery(id+"F0.wireOp",EDGE,"E0.right"),sQuery(id+"F0.wireOp",EDGE,"E2.filletArc"),sQuery(id+"F0.wireOp",EDGE,"E3"),sQuery(id+"F0.wireOp",EDGE,"E4.filletArc"),sQuery(id+"F0.wireOp",EDGE,"E8"),sQuery(id+"F0.wireOp",EDGE,"E9"),sQuery(id+"F0.wireOp",EDGE,"E12"),sQuery(id+"F0.wireOp",EDGE,"E13.trimOffspring"),sQuery(id+"F0.wireOp",EDGE,"E14.trimOffspring"),sQuery(id+"F0.wireOp",EDGE,"E15.filletArc"),sQuery(id+"F0.wireOp",EDGE,"E17"),sQuery(id+"F0.wireOp",EDGE,"E19"),sQuery(id+"F0.wireOp",EDGE,"E20"),sQuery(id+"F0.wireOp",EDGE,"E21"),sQuery(id+"F0.wireOp",EDGE,"E22"),sQuery(id+"F0.wireOp",EDGE,"E23.filletArc"),sQuery(id+"F0.wireOp",EDGE,"E24.filletArc"),sQuery(id+"F0.wireOp",EDGE,"E25.filletArc"),sQuery(id+"F0.wireOp",EDGE,"E26.filletArc"),sQuery(id+"F0.wireOp",EDGE,"E27.filletArc"),sQuery(id+"F0.wireOp",EDGE,"E28"),sQuery(id+"F0.wireOp",EDGE,"E30"),sQuery(id+"F0.wireOp",EDGE,"E32"),sQuery(id+"F0.wireOp",EDGE,"E33"),sQuery(id+"F0.wireOp",EDGE,"E34.filletArc"),sQuery(id+"F0.wireOp",EDGE,"E35.filletArc"),sQuery(id+"F0.wireOp",EDGE,"E36"),sQuery(id+"F0.wireOp",EDGE,"E41"),sQuery(id+"F0.wireOp",EDGE,"E42"),sQuery(id+"F0.wireOp",EDGE,"E43"),sQuery(id+"F0.wireOp",EDGE,"E44"),sQuery(id+"F0.wireOp",EDGE,"E45.1.0"),sQuery(id+"F0.wireOp",EDGE,"E45.1.1"),sQuery(id+"F0.wireOp",EDGE,"E45.1.2"),sQuery(id+"F0.wireOp",EDGE,"E45.1.3"),sQuery(id+"F0.wireOp",EDGE,"E45.2.0"),sQuery(id+"F0.wireOp",EDGE,"E45.2.1"),sQuery(id+"F0.wireOp",EDGE,"E45.2.2"),sQuery(id+"F0.wireOp",EDGE,"E45.2.3"),sQuery(id+"F0.wireOp",EDGE,"E45.3.0"),sQuery(id+"F0.wireOp",EDGE,"E45.3.1"),sQuery(id+"F0.wireOp",EDGE,"E45.3.2"),sQuery(id+"F0.wireOp",EDGE,"E45.3.3"),sQuery(id+"F0.wireOp",EDGE,"E47"),sQuery(id+"F0.wireOp",EDGE,"E48"),sQuery(id+"F0.wireOp",EDGE,"E49"),sQuery(id+"F0.wireOp",EDGE,"E50"),sQuery(id+"F0.wireOp",EDGE,"E51.1.0"),sQuery(id+"F0.wireOp",EDGE,"E51.1.1"),sQuery(id+"F0.wireOp",EDGE,"E51.1.2"),sQuery(id+"F0.wireOp",EDGE,"E51.1.3"),sQuery(id+"F0.wireOp",EDGE,"E51.2.0"),sQuery(id+"F0.wireOp",EDGE,"E51.2.1"),sQuery(id+"F0.wireOp",EDGE,"E51.2.2"),sQuery(id+"F0.wireOp",EDGE,"E51.2.3"),sQuery(id+"F0.wireOp",EDGE,"E51.3.0"),sQuery(id+"F0.wireOp",EDGE,"E51.3.1"),sQuery(id+"F0.wireOp",EDGE,"E51.3.2"),sQuery(id+"F0.wireOp",EDGE,"E51.3.3"),sQuery(id+"F0.wireOp",EDGE,"E52.MirrorCS"),sQuery(id+"F0.wireOp",EDGE,"E53.MirrorCS"),sQuery(id+"F0.wireOp",EDGE,"E54.MirrorCS"),sQuery(id+"F0.wireOp",EDGE,"E55.MirrorCS"),sQuery(id+"F0.wireOp",EDGE,"E56.MirrorCS"),sQuery(id+"F0.wireOp",EDGE,"E57.MirrorCS"),sQuery(id+"F0.wireOp",EDGE,"E58.MirrorCS"),sQuery(id+"F0.wireOp",EDGE,"E59.MirrorCS"),sQuery(id+"F0.wireOp",EDGE,"E60.MirrorCS"),sQuery(id+"F0.wireOp",EDGE,"E61.MirrorCS"),sQuery(id+"F0.wireOp",EDGE,"E62.MirrorCS"),sQuery(id+"F0.wireOp",EDGE,"E63.MirrorCS"),sQuery(id+"F0.wireOp",EDGE,"E64.MirrorCS"),sQuery(id+"F0.wireOp",EDGE,"E65.MirrorCS"),sQuery(id+"F0.wireOp",EDGE,"E66.MirrorCS"),sQuery(id+"F0.wireOp",EDGE,"E67.MirrorCS"),sQuery(id+"F0.wireOp",EDGE,"E68.MirrorCS"),sQuery(id+"F0.wireOp",EDGE,"E69.MirrorCS"),sQuery(id+"F0.wireOp",EDGE,"E70.MirrorCS"),sQuery(id+"F0.wireOp",EDGE,"E71.MirrorCS"),sQuery(id+"F0.wireOp",EDGE,"E72.MirrorCS"),sQuery(id+"F0.wireOp",EDGE,"E73.MirrorCS"),sQuery(id+"F0.wireOp",EDGE,"E74.MirrorCS"),sQuery(id+"F0.wireOp",EDGE,"E75.MirrorCS"),sQuery(id+"F0.wireOp",EDGE,"E76.MirrorCS"),sQuery(id+"F0.wireOp",EDGE,"E77.MirrorCS"),sQuery(id+"F0.wireOp",EDGE,"E78.MirrorCS"),sQuery(id+"F0.wireOp",EDGE,"E79.MirrorCS"),sQuery(id+"F0.wireOp",EDGE,"E80.MirrorCS"),sQuery(id+"F0.wireOp",EDGE,"E81.MirrorC"),sQuery(id+"F0.wireOp",EDGE,"E82.MirrorC"),sQuery(id+"F0.wireOp",EDGE,"E83.MirrorCS"),sQuery(id+"F0.wireOp",EDGE,"E84.MirrorCS"),sQuery(id+"F0.wireOp",EDGE,"E85.MirrorCS"),sQuery(id+"F0.wireOp",EDGE,"E86.MirrorCS"),sQuery(id+"F0.wireOp",EDGE,"E87.MirrorCS"),sQuery(id+"F0.wireOp",EDGE,"E88.MirrorCS"),sQuery(id+"F0.wireOp",EDGE,"E89.MirrorCS"),sQuery(id+"F0.wireOp",EDGE,"E90.MirrorCS"),sQuery(id+"F0.wireOp",EDGE,"E92.MirrorCS"),sQuery(id+"F0.wireOp",EDGE,"E93.MirrorCS"),sQuery(id+"F0.wireOp",EDGE,"E96.MirrorCS"),sQuery(id+"F0.wireOp",EDGE,"E97.MirrorCS"),sQuery(id+"F0.wireOp",EDGE,"E99.MirrorCS"),sQuery(id+"F0.wireOp",EDGE,"E100.MirrorCS"),sQuery(id+"F0.wireOp",EDGE,"E103.MirrorC"),sQuery(id+"F0.wireOp",EDGE,"E106.MirrorCS"),sQuery(id+"F0.wireOp",EDGE,"E107.MirrorCS"),sQuery(id+"F0.wireOp",EDGE,"E109.MirrorCS"),sQuery(id+"F0.wireOp",EDGE,"E110.MirrorC"),sQuery(id+"F0.wireOp",EDGE,"E111.MirrorCS"),sQuery(id+"F0.wireOp",EDGE,"E114.MirrorCS"),sQuery(id+"F0.wireOp",EDGE,"E116.MirrorCS"),sQuery(id+"F0.wireOp",EDGE,"E117.MirrorCS"),sQuery(id+"F0.wireOp",EDGE,"E118.MirrorCS"),sQuery(id+"F0.wireOp",EDGE,"E119.MirrorCS"),sQuery(id+"F0.wireOp",EDGE,"E121.MirrorCS"),sQuery(id+"F0.wireOp",EDGE,"E123.MirrorCS"),sQuery(id+"F0.wireOp",EDGE,"E124.MirrorCS"),sQuery(id+"F0.wireOp",EDGE,"E125.MirrorCS"),sQuery(id+"F0.wireOp",EDGE,"E126.MirrorCS"),sQuery(id+"F0.wireOp",EDGE,"E127"),sQuery(id+"F0.wireOp",EDGE,"E128.0.1.0"),sQuery(id+"F0.wireOp",EDGE,"E128.1.0.0"),sQuery(id+"F0.wireOp",EDGE,"E128.1.1.0"),sQuery(id+"F0.wireOp",EDGE,"E129"),sQuery(id+"F0.wireOp",EDGE,"E130.0.1.0"),sQuery(id+"F0.wireOp",EDGE,"E130.1.0.0"),sQuery(id+"F0.wireOp",EDGE,"E130.1.1.0"),sQuery(id+"F0.wireOp",EDGE,"2X2VCuhx-sfNE-qQAx-ANOA-V8PgWdT9DL1t"),sQuery(id+"F0.wireOp",EDGE,"EbufiATG-6Epo-heG6-67Bm-3WETjLEGOB6e"),sQuery(id+"F0.wireOp",EDGE,"E131"),sQuery(id+"F0.wireOp",EDGE,"E132.MirrorC")])],"isStart":false});
            var sketch = newSketch(context, id + "F6", { "sketchPlane" : qUnion([Q0])});
            skCircle(sketch, "E167", {"center": v(-65, 0) * mm, "radius": 8 * mm});
            skPoint(sketch, "E167.centerSnap0", {"position": v(-69, 0) * mm});
            skArc(sketch, "E168", {"start": v(-59.85, -15.85) * mm, "mid": v(-57.5, -17.5) * mm, "end": v(-55.15, -15.85) * mm});
            skArc(sketch, "E169", {"start": v(-55.15, 15.85) * mm, "mid": v(-57.5, 17.5) * mm, "end": v(-59.85, 15.85) * mm});
            skLineSegment(sketch, "E170", {"start": v(-59.85, -15.85) * mm, "end": v(-55.15, -15.85) * mm});
            skLineSegment(sketch, "E171", {"start": v(-59.85, 15.85) * mm, "end": v(-55.15, 15.85) * mm});
            skSolve(sketch);
        }
        {
            var Q0;
            Q0=qSketchRegion(id+"F6",true);
            extrude(context, id + "F7", {"entities" : qUnion([Q0]), "operationType" : NewBodyOperationType.ADD, "oppositeDirection" : true, "depth" : 4 * mm});
        }
        {
            var Q0;
            Q0=makeQuery(id+"F7.boolean.opBoolean","INTERSECT",EDGE,{"disambiguationData":[OD(0.0)],"derivedFrom":[makeQuery(id+"F1.opExtrude","SWEPT_FACE",FACE,{"disambiguationData":[OSD([sQuery(id+"F0.wireOp",EDGE,"E0.left"),sQuery(id+"F0.wireOp",EDGE,"E92.MirrorCS")])]}),makeQuery(id+"F7.opExtrude","SWEPT_FACE",FACE,{"disambiguationData":[OSD([sQuery(id+"F6.wireOp",EDGE,"E167")])]})]});
            var Q1;
            Q1=makeQuery(id+"F7.boolean.opBoolean","INTERSECT",EDGE,{"disambiguationData":[OD(1.0)],"derivedFrom":[makeQuery(id+"F1.opExtrude","SWEPT_FACE",FACE,{"disambiguationData":[OSD([sQuery(id+"F0.wireOp",EDGE,"E0.left"),sQuery(id+"F0.wireOp",EDGE,"E92.MirrorCS")])]}),makeQuery(id+"F7.opExtrude","SWEPT_FACE",FACE,{"disambiguationData":[OSD([sQuery(id+"F6.wireOp",EDGE,"E167")])]})]});
            var Q2;
            Q2=makeQuery(id+"F7.boolean.opBoolean","INTERSECT",EDGE,{"disambiguationData":[OD(0.0)],"derivedFrom":[makeQuery(id+"F1.opExtrude","SWEPT_FACE",FACE,{"disambiguationData":[OSD([sQuery(id+"F0.wireOp",EDGE,"E14.trimOffspring")])]}),makeQuery(id+"F7.opExtrude","SWEPT_FACE",FACE,{"disambiguationData":[OSD([sQuery(id+"F6.wireOp",EDGE,"E169")])]})]});
            var Q3;
            Q3=makeQuery(id+"F7.boolean.opBoolean","INTERSECT",EDGE,{"disambiguationData":[OD(1.0)],"derivedFrom":[makeQuery(id+"F1.opExtrude","SWEPT_FACE",FACE,{"disambiguationData":[OSD([sQuery(id+"F0.wireOp",EDGE,"E14.trimOffspring")])]}),makeQuery(id+"F7.opExtrude","SWEPT_FACE",FACE,{"disambiguationData":[OSD([sQuery(id+"F6.wireOp",EDGE,"E169")])]})]});
            var Q4;
            Q4=makeQuery(id+"F7.boolean.opBoolean","INTERSECT",EDGE,{"disambiguationData":[OD(0.0)],"derivedFrom":[makeQuery(id+"F1.opExtrude","SWEPT_FACE",FACE,{"disambiguationData":[OSD([sQuery(id+"F0.wireOp",EDGE,"E111.MirrorCS")])]}),makeQuery(id+"F7.opExtrude","SWEPT_FACE",FACE,{"disambiguationData":[OSD([sQuery(id+"F6.wireOp",EDGE,"E168")])]})]});
            var Q5;
            Q5=makeQuery(id+"F7.boolean.opBoolean","INTERSECT",EDGE,{"disambiguationData":[OD(1.0)],"derivedFrom":[makeQuery(id+"F1.opExtrude","SWEPT_FACE",FACE,{"disambiguationData":[OSD([sQuery(id+"F0.wireOp",EDGE,"E111.MirrorCS")])]}),makeQuery(id+"F7.opExtrude","SWEPT_FACE",FACE,{"disambiguationData":[OSD([sQuery(id+"F6.wireOp",EDGE,"E168")])]})]});
            fillet(context, id + "F8", {"entities" : qUnion([Q0, Q1, Q2, Q3, Q4, Q5]), "radius" : 5 * mm, "tangentPropagation" : true, "allowEdgeOverflow" : false});
        }
    });
